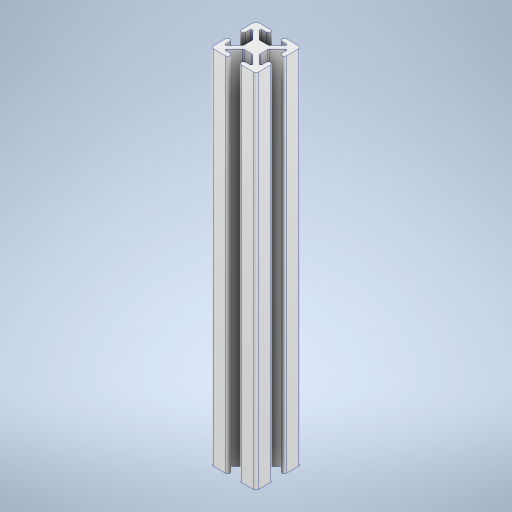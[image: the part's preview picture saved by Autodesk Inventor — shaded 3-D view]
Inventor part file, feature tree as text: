
AUTODESK INVENTOR PART (.ipt)
format: ipt  version: 2024 (Build 280153000, 153)  size: 346,624 bytes
history: native  units: in
note: dims shown in document units (in); Inventor stores cm internally (conversion verified against a paired STEP export)
features: fillet x2, extrude x1, sketch x1
ambient origin geometry x8: Origin, YZ Plane, XZ Plane, XY Plane, X Axis, Y Axis, Z Axis, Center Point
bodies: Solid1 (feature_tree)
feature tree (4):
  extrude  "Extrusion1"  Depth=1.0in
  fillet  "Fillet1"  Radius=0.8in
  fillet  "Fillet2"  Radius=0.8in
  sketch  "Sketch1"  dims[d0=1.0in d1=1.0in d2=0.8in d3=0.8in d4=0.35in d5=0.35in d6=0.125in d7=0.25in d8=0.125in d9=0.25in d10=0.1in d11=0.1in d12=8.0in d13=0.0in d14=0.05in d15=0.025in]
